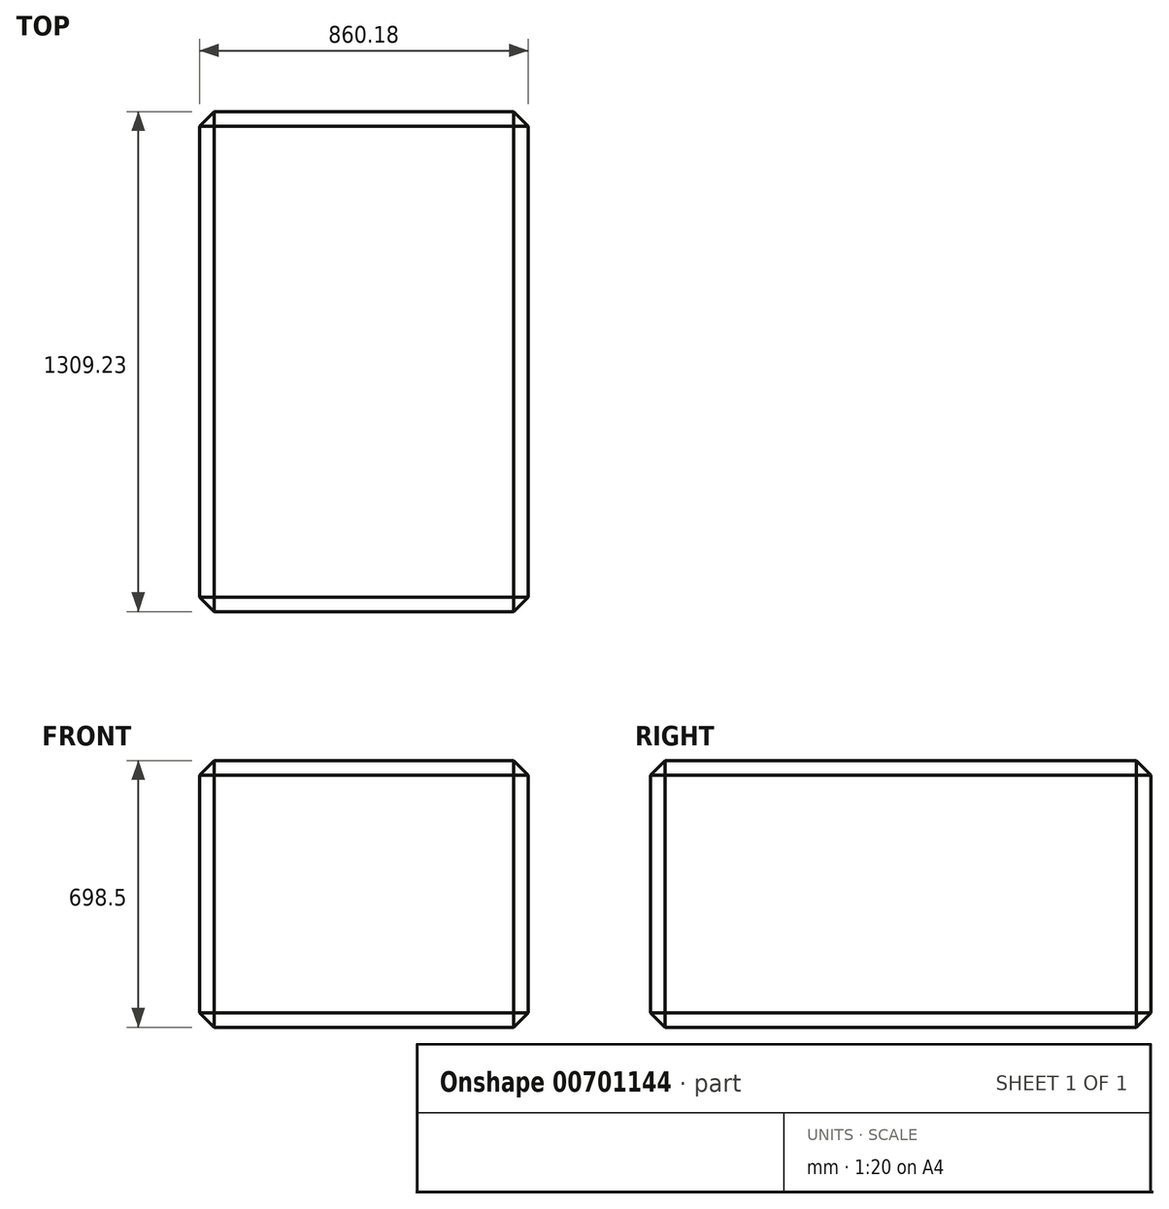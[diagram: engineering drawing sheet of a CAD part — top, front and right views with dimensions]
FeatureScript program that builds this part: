
annotation { "Feature Type Name" : "Feature", "Feature Type Description" : "" }
export const myFeature = defineFeature(function(context is Context, id is Id, definition is map)
    precondition{}
    {
        {
            var Q0;
            Q0=qCreatedBy(makeId("Top.planeOp"),FACE);
            var sketch = newSketch(context, id + "F0", { "sketchPlane" : qUnion([Q0])});
            skLineSegment(sketch, "E0.bottom", {"start": v(348.99, 441.28) * mm, "end": v(-511.2, 441.28) * mm});
            skLineSegment(sketch, "E0.top", {"start": v(348.99, -867.95) * mm, "end": v(-511.2, -867.95) * mm});
            skLineSegment(sketch, "E0.left", {"start": v(348.99, 441.28) * mm, "end": v(348.99, -867.95) * mm});
            skLineSegment(sketch, "E0.right", {"start": v(-511.2, 441.28) * mm, "end": v(-511.2, -867.95) * mm});
            skSolve(sketch);
        }
        {
            var Q0;
            Q0=makeQuery(id+"F0.imprint","IMPRINT",FACE,{"disambiguationData":[TD([[makeQuery(id+"F0.imprint","IMPRINT",EDGE,{"derivedFrom":sQuery(id+"F0.wireOp",EDGE,"E0.bottom")}),1.0]])]});
            extrude(context, id + "F1", {"entities" : qUnion([Q0]), "depth" : 698.5 * mm, "offsetDistance" : 25.4 * mm});
        }
        {
            var Q0;
            Q0=makeQuery(id+"F1.opExtrude","SWEPT_FACE",FACE,{"disambiguationData":[OSD([sQuery(id+"F0.wireOp",EDGE,"E0.bottom")])]});
            var Q1;
            Q1=makeQuery(id+"F1.opExtrude","SWEPT_FACE",FACE,{"disambiguationData":[OSD([sQuery(id+"F0.wireOp",EDGE,"E0.right")])]});
            var Q2;
            Q2=makeQuery(id+"F1.opExtrude","SWEPT_FACE",FACE,{"disambiguationData":[OSD([sQuery(id+"F0.wireOp",EDGE,"E0.top")])]});
            var Q3;
            Q3=makeQuery(id+"F1.opExtrude","SWEPT_FACE",FACE,{"disambiguationData":[OSD([sQuery(id+"F0.wireOp",EDGE,"E0.left")])]});
            chamfer(context, id + "F2", {"entities" : qUnion([Q0, Q1, Q2, Q3]), "width" : 38.1 * mm, "tangentPropagation" : true});
        }
    });
